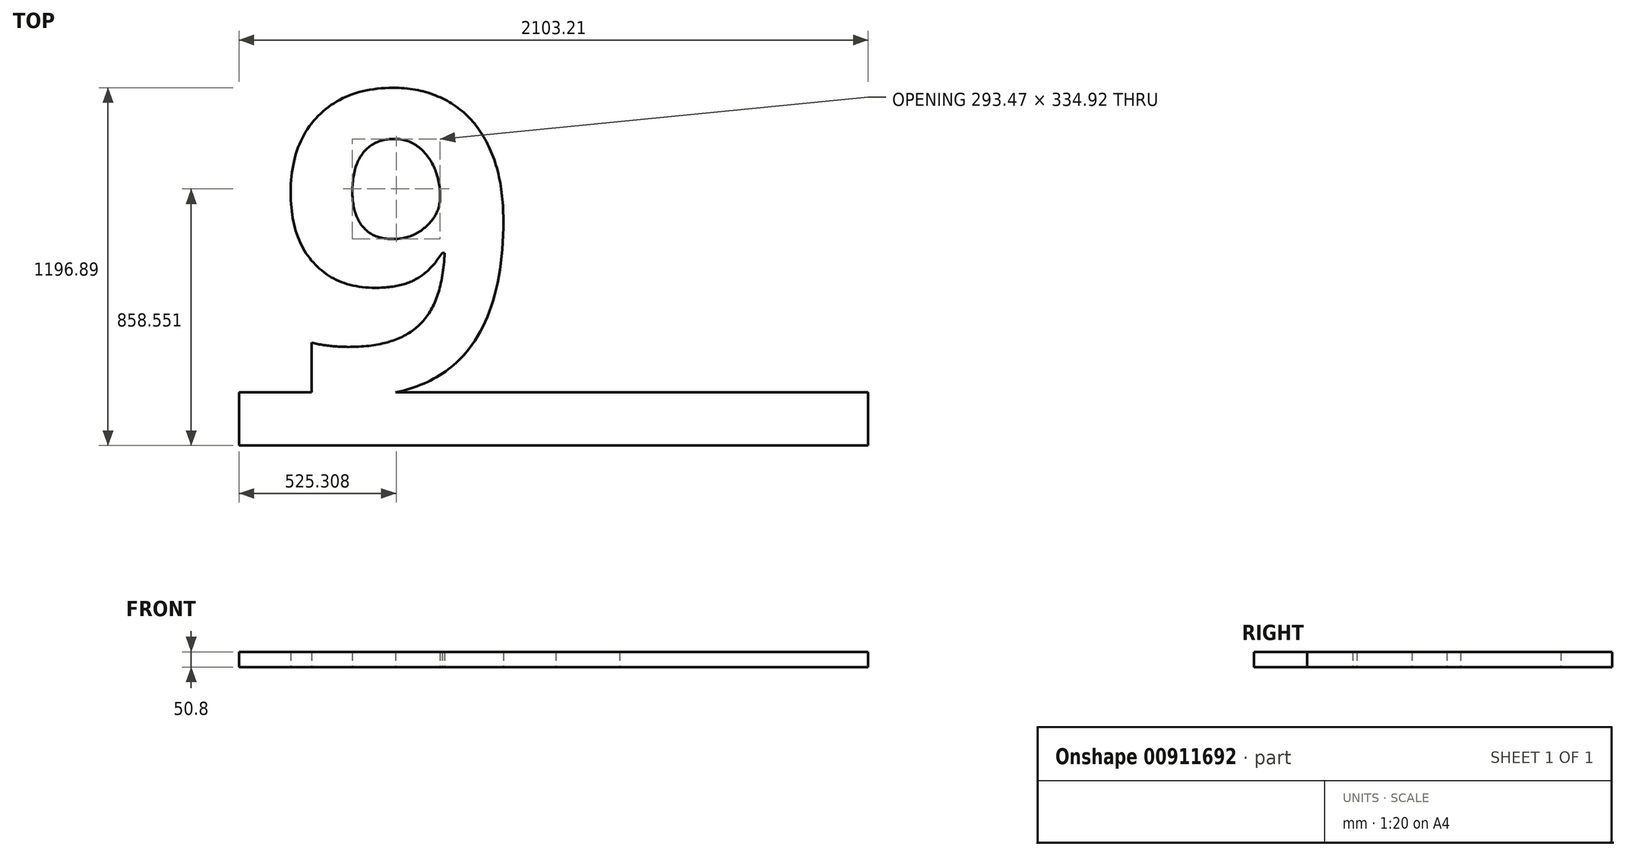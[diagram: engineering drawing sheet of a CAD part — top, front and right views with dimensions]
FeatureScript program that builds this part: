
annotation { "Feature Type Name" : "Feature", "Feature Type Description" : "" }
export const myFeature = defineFeature(function(context is Context, id is Id, definition is map)
    precondition{}
    {
        {
            var Q0;
            Q0=qCreatedBy(makeId("Top.planeOp"),FACE);
            var sketch = newSketch(context, id + "F0", { "sketchPlane" : qUnion([Q0])});
            skLineSegment(sketch, "E0.bottom", {"start": v(-428.81, -706.29) * mm, "end": v(1674.4, -706.29) * mm});
            skLineSegment(sketch, "E0.top", {"start": v(-428.81, -528.49) * mm, "end": v(1674.4, -528.49) * mm});
            skLineSegment(sketch, "E0.left", {"start": v(-428.81, -706.29) * mm, "end": v(-428.81, -528.49) * mm});
            skLineSegment(sketch, "E0.right", {"start": v(1674.4, -706.29) * mm, "end": v(1674.4, -528.49) * mm});
            skText(sketch, "E1", { "text": "9H", "fontName": "OpenSans-Bold.ttf"});
            const initialGuessF0  = {"E1": [-0.30181, -0.52849, 1, 0, 1.016]};
            skSetInitialGuess(sketch, initialGuessF0);
            skSolve(sketch);
        }
        {
            var Q0;
            Q0=makeQuery(id+"F0.imprint","IMPRINT",FACE,{"disambiguationData":[TD([[makeQuery(id+"F0.imprint","IMPRINT",EDGE,{"derivedFrom":sQuery(id+"F0.wireOp",EDGE,"86c1ac7c-6dd4-47f2-8f3d-e4d4cef76d82.sketch_text.stroke-0")}),-1.0]])]});
            var Q1;
            {var subQ1=sQuery(id+"F0.wireOp",EDGE,"86c1ac7c-6dd4-47f2-8f3d-e4d4cef76d82.sketch_text.stroke-32");Q1=makeQuery(id+"F0.imprint","IMPRINT",FACE,{"disambiguationData":[TD([[makeQuery(id+"F0.imprint","IMPRINT",EDGE,{"derivedFrom":subQ1}),-1.0]])]});}
            var Q2;
            Q2=makeQuery(id+"F0.imprint","IMPRINT",FACE,{"disambiguationData":[TD([[makeQuery(id+"F0.imprint","IMPRINT",EDGE,{"derivedFrom":sQuery(id+"F0.wireOp",EDGE,"E0.bottom")}),1.0]])]});
            var Q3;
            {var subQ0=sQuery(id+"F0.wireOp",EDGE,"86c1ac7c-6dd4-47f2-8f3d-e4d4cef76d82.sketch_text.stroke-8");var subQ1=sQuery(id+"F0.wireOp",EDGE,"86c1ac7c-6dd4-47f2-8f3d-e4d4cef76d82.sketch_text.stroke-7");var subQ2=makeQuery(id+"F0.imprint","INTERSECT",VERTEX,{"derivedFrom":[subQ1,subQ0]});Q3=makeQuery(id+"F0.imprint","IMPRINT",FACE,{"disambiguationData":[TD([[makeQuery(id+"F0.imprint","IMPRINT",EDGE,{"disambiguationData":[TD([[subQ2,1.0]])],"derivedFrom":subQ1}),-1.0]])]});}
            var Q4;
            Q4=makeQuery(id+"F0.imprint","IMPRINT",FACE,{"disambiguationData":[TD([[makeQuery(id+"F0.imprint","IMPRINT",EDGE,{"derivedFrom":sQuery(id+"F0.wireOp",EDGE,"E1.sketch_text.stroke-26")}),-1.0]])]});
            var Q5;
            {var subQ1=sQuery(id+"F0.wireOp",EDGE,"E1.sketch_text.stroke-0");Q5=makeQuery(id+"F0.imprint","IMPRINT",FACE,{"disambiguationData":[TD([[makeQuery(id+"F0.imprint","IMPRINT",EDGE,{"derivedFrom":subQ1}),-1.0]])]});}
            var Q6;
            {var subQ5=sQuery(id+"F0.wireOp",EDGE,"E1.sketch_text.stroke-2");Q6=makeQuery(id+"F0.imprint","IMPRINT",FACE,{"disambiguationData":[TD([[makeQuery(id+"F0.imprint","IMPRINT",EDGE,{"derivedFrom":subQ5}),-1.0]])]});}
            extrude(context, id + "F1", {"entities" : qUnion([Q0, Q1, Q2, Q3, Q4, Q5, Q6]), "depth" : 50.8 * mm, "offsetDistance" : 25.4 * mm});
        }
    });
